# Revit family: Medical_All_Hill-Rom_Compella
name_source: partatom
category: Specialty Equipment
revit_build: Autodesk Revit Architecture 2015 (Build: 20140606_1530(x64)
units: mm (PartAtom-declared; Revit-internal decimal feet)

## types (1)
- Compella
    Actual Foot Angle = 0.25°
    Actual Head Angle = 0.25°
    Apparent Load = 0 VA
    Assembly Code = E1020810
    BIMobject category = All
    BIMobject category code = medical-all
    BIMobject main category = Medical
    BIMobject main category code = medical
    Brand url = https://construction.hill-rom.com
    Controls = Plastic-Hill-Rom-Light Blue
    Date of publishing = 4/1/2018
    Description = Full Featured Hospital Bed
    Design country = United States
    Edition number = 1
    Finish = Plastic-Hill-Rom-Light Beige
    Foot Angle = 0.00°
    Frequency = 0 Hz
    Frequency Range = 50-60 Hz
    Head Angle = 0.00°
    Height = 2' - 11"
    IFC Classification = Furniture
    Installation instructions = https://construction.hill-rom.com
    Length = 7' - 4"
    Manufacturer = Hill-Rom Co.
    Manufacturer country = United States
    Manufacturer name = Hill-Rom
    Masterformat 2014 Code = 12 54 00
    Masterformat 2014 Description = Hospitality Furniture
    Mattress = Textile-Hill-Rom-Mattress
    Mattress Height = 0' - 7 27/32"
    Max Amperage = 12 A
    Model = Compella Bed System
    Nominal height = 0' - 0"
    Nominal width = 0' - 0"
    OmniClass Code = 23-25 45 11 11
    OmniClass Description = Patient Beds
    Power Factor = 1
    Product Documentation Link = http://www.hill-rom.com
    Product Guid = ecaee835-56ed-4e3c-b811-41850f660bd7
    Product Page URL = http://www.hill-rom.com
    Product SKU = Compella-Bariatric-Bed
    Product certification = https://www.hill-rom.com
    Product data url = https://bimobject.com
    Product family = Patient Beds
    Product group = CareAssist® ES Medical Surgical Hospital Bed
    Product url = https://www.hill-rom.com
    QR code = http://bimobject.com
    Style = Bariatric
    Technical description = https://construction.hill-rom.com
    Type Comments = Bariatric Bed System
    UNSPSC Code = 56
    URL = www.hill-rom.com
    Uniclass 1.4 Code = L8522
    Uniclass 1.4 Description = Hospital beds
    Uniclass 2015 Code = Pr_40_50_06_39
    Uniclass 2015 Name = Hospital beds
    Voltage = 120 V
    Voltage Range = 120-230 V
    Weight Net (Kg) = 0
    Wheels = Plastic-Hill-Rom-Dark Grey
    Width = 3' - 11 7/32"
    Youtube clip = https://www.hill-rom.ca

## geometry (parser evidence)
native form markers: Blend x16, Sweep x18
no freeform markers — native parametric forms only
